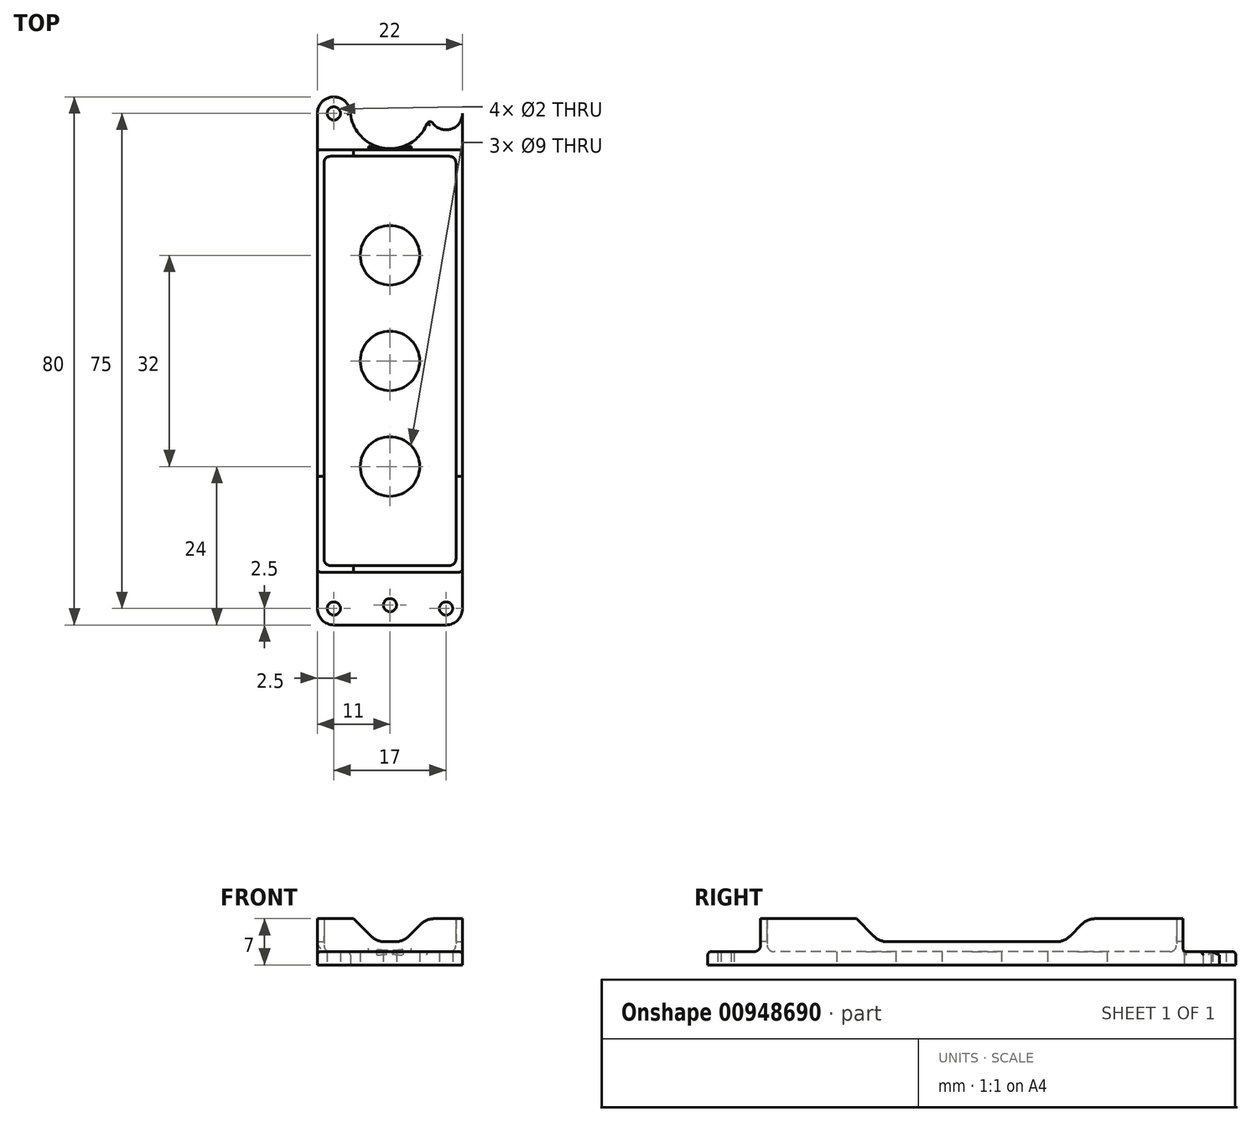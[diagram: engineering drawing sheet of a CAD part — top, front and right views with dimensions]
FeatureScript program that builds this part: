
annotation { "Feature Type Name" : "Feature", "Feature Type Description" : "" }
export const myFeature = defineFeature(function(context is Context, id is Id, definition is map)
    precondition{}
    {
        {
            var Q0;
            Q0=qCreatedBy(makeId("Top.planeOp"),FACE);
            var sketch = newSketch(context, id + "F0", { "sketchPlane" : qUnion([Q0])});
            skPoint(sketch, "E0.middle", {"position": v(0, 0) * mm});
            skPoint(sketch, "E1", {"position": v(-8, 8) * mm});
            skPoint(sketch, "E2", {"position": v(8, 8) * mm});
            skPoint(sketch, "E3", {"position": v(8, -8) * mm});
            skPoint(sketch, "E4", {"position": v(-8, -8) * mm});
            skLineSegment(sketch, "E5", {"start": v(0, -40) * mm, "end": v(8.5, -40) * mm});
            skLineSegment(sketch, "E6", {"start": v(11, -37.5) * mm, "end": v(11, -25.31) * mm});
            skLineSegment(sketch, "E7", {"start": v(-11, 37.5) * mm, "end": v(-11, 25.31) * mm});
            skLineSegment(sketch, "E8", {"start": v(-8.5, -40) * mm, "end": v(0, -40) * mm});
            skLineSegment(sketch, "E9.trimOffspring", {"start": v(11, 25.31) * mm, "end": v(11, 37.5) * mm});
            skLineSegment(sketch, "E10.trimOffspring", {"start": v(-11, -25.31) * mm, "end": v(-11, -37.5) * mm});
            skArc(sketch, "E11.filletArc", {"start": v(-8.5, 40) * mm, "mid": v(-10.27, 39.27) * mm, "end": v(-11, 37.5) * mm});
            skPoint(sketch, "E12.visualSharp", {"position": v(11, 40) * mm});
            skArc(sketch, "E12.filletArc", {"start": v(11, 37.5) * mm, "mid": v(10.27, 39.27) * mm, "end": v(8.5, 40) * mm});
            skArc(sketch, "E13.filletArc", {"start": v(-11, -37.5) * mm, "mid": v(-10.27, -39.27) * mm, "end": v(-8.5, -40) * mm});
            skPoint(sketch, "E14.visualSharp", {"position": v(11, -40) * mm});
            skArc(sketch, "E14.filletArc", {"start": v(8.5, -40) * mm, "mid": v(10.27, -39.27) * mm, "end": v(11, -37.5) * mm});
            skCircle(sketch, "E15", {"center": v(-8.5, 37.5) * mm, "radius": 2.5 * mm});
            skCircle(sketch, "E16", {"center": v(8.5, 37.5) * mm, "radius": 2.5 * mm});
            skCircle(sketch, "E17", {"center": v(-8.5, -37.5) * mm, "radius": 2.5 * mm});
            skCircle(sketch, "E18", {"center": v(8.5, -37.5) * mm, "radius": 2.5 * mm});
            skPoint(sketch, "E19", {"position": v(0, 30) * mm});
            skPoint(sketch, "E20", {"position": v(0, 16) * mm});
            skPoint(sketch, "E21.MirrorP", {"position": v(0, -16) * mm});
            skPoint(sketch, "E22.MirrorP", {"position": v(0, -30) * mm});
            skLineSegment(sketch, "E23", {"start": v(-11, 25.31) * mm, "end": v(-11, -25.31) * mm});
            skLineSegment(sketch, "E24", {"start": v(11, 25.31) * mm, "end": v(11, -25.31) * mm});
            skArc(sketch, "E25", {"start": v(-6, 37.43) * mm, "mid": v(0, 32.15) * mm, "end": v(6, 37.43) * mm});
            skPoint(sketch, "E25.centerSnap0", {"position": v(0, 40) * mm});
            skLineSegment(sketch, "E26", {"start": v(0, -32) * mm, "end": v(11, -32) * mm});
            skLineSegment(sketch, "E27", {"start": v(0, -32) * mm, "end": v(-11, -32) * mm});
            skLineSegment(sketch, "E28", {"start": v(0, 32) * mm, "end": v(11, 32) * mm});
            skLineSegment(sketch, "E29", {"start": v(0, 32) * mm, "end": v(-11, 32) * mm});
            skLineSegment(sketch, "E30", {"start": v(0, -31) * mm, "end": v(10, -31) * mm});
            skLineSegment(sketch, "E31", {"start": v(10, -31) * mm, "end": v(10, 31) * mm});
            skLineSegment(sketch, "E32", {"start": v(10, 31) * mm, "end": v(-10, 31) * mm});
            skLineSegment(sketch, "E33", {"start": v(-10, 31) * mm, "end": v(-10, -31) * mm});
            skLineSegment(sketch, "E34", {"start": v(-10, -31) * mm, "end": v(0, -31) * mm});
            skPoint(sketch, "E35", {"position": v(0, -37) * mm});
            skSolve(sketch);
        }
        {
            var Q0;
            {var subQ0=sQuery(id+"F0.wireOp",EDGE,"E15");var subQ1=makeQuery(id+"F0.imprint","INTERSECT",VERTEX,{"derivedFrom":[sQuery(id+"F0.wireOp",EDGE,"E7"),subQ0]});Q0=makeQuery(id+"F0.imprint","IMPRINT",FACE,{"disambiguationData":[TD([[makeQuery(id+"F0.imprint","IMPRINT",EDGE,{"disambiguationData":[TD([[subQ1,-1.0]])],"derivedFrom":subQ0}),1.0]])]});}
            var Q1;
            {var subQ3=sQuery(id+"F0.wireOp",EDGE,"E25");Q1=makeQuery(id+"F0.imprint","IMPRINT",FACE,{"disambiguationData":[TD([[makeQuery(id+"F0.imprint","IMPRINT",EDGE,{"derivedFrom":subQ3}),-1.0]])]});}
            var Q2;
            {var subQ0=sQuery(id+"F0.wireOp",EDGE,"E16");var subQ1=makeQuery(id+"F0.imprint","INTERSECT",VERTEX,{"derivedFrom":[sQuery(id+"F0.wireOp",EDGE,"E9.trimOffspring"),subQ0]});Q2=makeQuery(id+"F0.imprint","IMPRINT",FACE,{"disambiguationData":[TD([[makeQuery(id+"F0.imprint","IMPRINT",EDGE,{"disambiguationData":[TD([[subQ1,-1.0]])],"derivedFrom":subQ0}),1.0]])]});}
            var Q3;
            {var subQ3=sQuery(id+"F0.wireOp",EDGE,"E23");Q3=makeQuery(id+"F0.imprint","IMPRINT",FACE,{"disambiguationData":[TD([[makeQuery(id+"F0.imprint","IMPRINT",EDGE,{"derivedFrom":subQ3}),1.0]])]});}
            var Q4;
            Q4=makeQuery(id+"F0.imprint","IMPRINT",FACE,{"disambiguationData":[TD([[makeQuery(id+"F0.imprint","IMPRINT",EDGE,{"derivedFrom":sQuery(id+"F0.wireOp",EDGE,"E30")}),1.0]])]});
            var Q5;
            {var subQ9=sQuery(id+"F0.wireOp",EDGE,"E5");Q5=makeQuery(id+"F0.imprint","IMPRINT",FACE,{"disambiguationData":[TD([[makeQuery(id+"F0.imprint","IMPRINT",EDGE,{"derivedFrom":subQ9}),1.0]])]});}
            var Q6;
            {var subQ0=sQuery(id+"F0.wireOp",EDGE,"E17");var subQ1=makeQuery(id+"F0.imprint","INTERSECT",VERTEX,{"derivedFrom":[sQuery(id+"F0.wireOp",EDGE,"E8"),subQ0]});Q6=makeQuery(id+"F0.imprint","IMPRINT",FACE,{"disambiguationData":[TD([[makeQuery(id+"F0.imprint","IMPRINT",EDGE,{"disambiguationData":[TD([[subQ1,1.0]])],"derivedFrom":subQ0}),1.0]])]});}
            var Q7;
            {var subQ0=sQuery(id+"F0.wireOp",EDGE,"E18");var subQ1=makeQuery(id+"F0.imprint","INTERSECT",VERTEX,{"derivedFrom":[sQuery(id+"F0.wireOp",EDGE,"E5"),subQ0]});Q7=makeQuery(id+"F0.imprint","IMPRINT",FACE,{"disambiguationData":[TD([[makeQuery(id+"F0.imprint","IMPRINT",EDGE,{"disambiguationData":[TD([[subQ1,1.0]])],"derivedFrom":subQ0}),1.0]])]});}
            extrude(context, id + "F1", {"entities" : qUnion([Q0, Q1, Q2, Q3, Q4, Q5, Q6, Q7]), "depth" : 2 * mm, "offsetDistance" : 25 * mm});
        }
        {
            var Q0;
            {var subQ3=sQuery(id+"F0.wireOp",EDGE,"E23");Q0=makeQuery(id+"F0.imprint","IMPRINT",FACE,{"disambiguationData":[TD([[makeQuery(id+"F0.imprint","IMPRINT",EDGE,{"derivedFrom":subQ3}),1.0]])]});}
            extrude(context, id + "F2", {"entities" : qUnion([Q0]), "operationType" : NewBodyOperationType.ADD, "depth" : 7 * mm, "offsetDistance" : 25 * mm});
        }
        {
            var Q0;
            Q0=makeQuery(id+"F1.opExtrude","CAP_EDGE",EDGE,{"disambiguationData":[OSD([sQuery(id+"F0.wireOp",EDGE,"E25")])],"isStart":false});
            fillet(context, id + "F3", {"entities" : qUnion([Q0]), "radius" : 0.5 * mm, "tangentPropagation" : true, "allowEdgeOverflow" : false});
        }
        {
            var Q0;
            Q0=makeQuery(id+"F2.boolean.opBoolean","INTERSECT",EDGE,{"derivedFrom":[makeQuery(id+"F1.opExtrude","CAP_FACE",FACE,{"disambiguationData":[OSD([sQuery(id+"F0.wireOp",EDGE,"E5"),sQuery(id+"F0.wireOp",EDGE,"E6"),sQuery(id+"F0.wireOp",EDGE,"E7"),sQuery(id+"F0.wireOp",EDGE,"E8"),sQuery(id+"F0.wireOp",EDGE,"E9.trimOffspring"),sQuery(id+"F0.wireOp",EDGE,"E10.trimOffspring"),sQuery(id+"F0.wireOp",EDGE,"E15"),sQuery(id+"F0.wireOp",EDGE,"E16"),sQuery(id+"F0.wireOp",EDGE,"E17"),sQuery(id+"F0.wireOp",EDGE,"E18"),sQuery(id+"F0.wireOp",EDGE,"E23"),sQuery(id+"F0.wireOp",EDGE,"E24"),sQuery(id+"F0.wireOp",EDGE,"E25")])],"isStart":false}),makeQuery(id+"F2.opExtrude","SWEPT_FACE",FACE,{"disambiguationData":[OSD([sQuery(id+"F0.wireOp",EDGE,"E26"),sQuery(id+"F0.wireOp",EDGE,"E27")])]})]});
            var Q1;
            Q1=makeQuery(id+"F2.opExtrude","SWEPT_EDGE",EDGE,{"disambiguationData":[OSD([sQuery(id+"F0.wireOp",EDGE,"E33"),sQuery(id+"F0.wireOp",EDGE,"E34")])]});
            var Q2;
            Q2=makeQuery(id+"F2.opExtrude","SWEPT_EDGE",EDGE,{"disambiguationData":[OSD([sQuery(id+"F0.wireOp",EDGE,"E30"),sQuery(id+"F0.wireOp",EDGE,"E31")])]});
            var Q3;
            Q3=makeQuery(id+"F2.boolean.opBoolean","INTERSECT",EDGE,{"derivedFrom":[makeQuery(id+"F1.opExtrude","CAP_FACE",FACE,{"disambiguationData":[OSD([sQuery(id+"F0.wireOp",EDGE,"E5"),sQuery(id+"F0.wireOp",EDGE,"E6"),sQuery(id+"F0.wireOp",EDGE,"E7"),sQuery(id+"F0.wireOp",EDGE,"E8"),sQuery(id+"F0.wireOp",EDGE,"E9.trimOffspring"),sQuery(id+"F0.wireOp",EDGE,"E10.trimOffspring"),sQuery(id+"F0.wireOp",EDGE,"E15"),sQuery(id+"F0.wireOp",EDGE,"E16"),sQuery(id+"F0.wireOp",EDGE,"E17"),sQuery(id+"F0.wireOp",EDGE,"E18"),sQuery(id+"F0.wireOp",EDGE,"E23"),sQuery(id+"F0.wireOp",EDGE,"E24"),sQuery(id+"F0.wireOp",EDGE,"E25")])],"isStart":false}),makeQuery(id+"F2.opExtrude","SWEPT_FACE",FACE,{"disambiguationData":[OSD([sQuery(id+"F0.wireOp",EDGE,"E30"),sQuery(id+"F0.wireOp",EDGE,"E34")])]})]});
            var Q4;
            Q4=makeQuery(id+"F2.boolean.opBoolean","INTERSECT",EDGE,{"derivedFrom":[makeQuery(id+"F1.opExtrude","CAP_FACE",FACE,{"disambiguationData":[OSD([sQuery(id+"F0.wireOp",EDGE,"E5"),sQuery(id+"F0.wireOp",EDGE,"E6"),sQuery(id+"F0.wireOp",EDGE,"E7"),sQuery(id+"F0.wireOp",EDGE,"E8"),sQuery(id+"F0.wireOp",EDGE,"E9.trimOffspring"),sQuery(id+"F0.wireOp",EDGE,"E10.trimOffspring"),sQuery(id+"F0.wireOp",EDGE,"E15"),sQuery(id+"F0.wireOp",EDGE,"E16"),sQuery(id+"F0.wireOp",EDGE,"E17"),sQuery(id+"F0.wireOp",EDGE,"E18"),sQuery(id+"F0.wireOp",EDGE,"E23"),sQuery(id+"F0.wireOp",EDGE,"E24"),sQuery(id+"F0.wireOp",EDGE,"E25")])],"isStart":false}),makeQuery(id+"F2.opExtrude","SWEPT_FACE",FACE,{"disambiguationData":[OSD([sQuery(id+"F0.wireOp",EDGE,"E33")])]})]});
            var Q5;
            Q5=makeQuery(id+"F2.boolean.opBoolean","INTERSECT",EDGE,{"derivedFrom":[makeQuery(id+"F1.opExtrude","CAP_FACE",FACE,{"disambiguationData":[OSD([sQuery(id+"F0.wireOp",EDGE,"E5"),sQuery(id+"F0.wireOp",EDGE,"E6"),sQuery(id+"F0.wireOp",EDGE,"E7"),sQuery(id+"F0.wireOp",EDGE,"E8"),sQuery(id+"F0.wireOp",EDGE,"E9.trimOffspring"),sQuery(id+"F0.wireOp",EDGE,"E10.trimOffspring"),sQuery(id+"F0.wireOp",EDGE,"E15"),sQuery(id+"F0.wireOp",EDGE,"E16"),sQuery(id+"F0.wireOp",EDGE,"E17"),sQuery(id+"F0.wireOp",EDGE,"E18"),sQuery(id+"F0.wireOp",EDGE,"E23"),sQuery(id+"F0.wireOp",EDGE,"E24"),sQuery(id+"F0.wireOp",EDGE,"E25")])],"isStart":false}),makeQuery(id+"F2.opExtrude","SWEPT_FACE",FACE,{"disambiguationData":[OSD([sQuery(id+"F0.wireOp",EDGE,"E31")])]})]});
            var Q6;
            Q6=makeQuery(id+"F2.opExtrude","SWEPT_EDGE",EDGE,{"disambiguationData":[OSD([sQuery(id+"F0.wireOp",EDGE,"E31"),sQuery(id+"F0.wireOp",EDGE,"E32")])]});
            var Q7;
            Q7=makeQuery(id+"F2.boolean.opBoolean","INTERSECT",EDGE,{"derivedFrom":[makeQuery(id+"F1.opExtrude","CAP_FACE",FACE,{"disambiguationData":[OSD([sQuery(id+"F0.wireOp",EDGE,"E5"),sQuery(id+"F0.wireOp",EDGE,"E6"),sQuery(id+"F0.wireOp",EDGE,"E7"),sQuery(id+"F0.wireOp",EDGE,"E8"),sQuery(id+"F0.wireOp",EDGE,"E9.trimOffspring"),sQuery(id+"F0.wireOp",EDGE,"E10.trimOffspring"),sQuery(id+"F0.wireOp",EDGE,"E15"),sQuery(id+"F0.wireOp",EDGE,"E16"),sQuery(id+"F0.wireOp",EDGE,"E17"),sQuery(id+"F0.wireOp",EDGE,"E18"),sQuery(id+"F0.wireOp",EDGE,"E23"),sQuery(id+"F0.wireOp",EDGE,"E24"),sQuery(id+"F0.wireOp",EDGE,"E25")])],"isStart":false}),makeQuery(id+"F2.opExtrude","SWEPT_FACE",FACE,{"disambiguationData":[OSD([sQuery(id+"F0.wireOp",EDGE,"E32")])]})]});
            var Q8;
            Q8=makeQuery(id+"F2.opExtrude","SWEPT_EDGE",EDGE,{"disambiguationData":[OSD([sQuery(id+"F0.wireOp",EDGE,"E32"),sQuery(id+"F0.wireOp",EDGE,"E33")])]});
            fillet(context, id + "F4", {"entities" : qUnion([Q0, Q1, Q2, Q3, Q4, Q5, Q6, Q7, Q8]), "radius" : 1 * mm, "tangentPropagation" : true, "allowEdgeOverflow" : false});
        }
        {
            var Q0;
            Q0=makeQuery(id+"F1.opExtrude","CAP_EDGE",EDGE,{"disambiguationData":[OSD([sQuery(id+"F0.wireOp",EDGE,"E15")])],"isStart":false});
            var Q1;
            Q1=makeQuery(id+"F1.opExtrude","CAP_EDGE",EDGE,{"disambiguationData":[OSD([sQuery(id+"F0.wireOp",EDGE,"E16")])],"isStart":false});
            var Q2;
            Q2=makeQuery(id+"F1.opExtrude","CAP_EDGE",EDGE,{"disambiguationData":[OSD([sQuery(id+"F0.wireOp",EDGE,"E5"),sQuery(id+"F0.wireOp",EDGE,"E8")])],"isStart":false});
            var Q3;
            Q3=makeQuery(id+"F2.boolean.opBoolean","INTERSECT",EDGE,{"derivedFrom":[makeQuery(id+"F1.opExtrude","CAP_FACE",FACE,{"disambiguationData":[OSD([sQuery(id+"F0.wireOp",EDGE,"E5"),sQuery(id+"F0.wireOp",EDGE,"E6"),sQuery(id+"F0.wireOp",EDGE,"E7"),sQuery(id+"F0.wireOp",EDGE,"E8"),sQuery(id+"F0.wireOp",EDGE,"E9.trimOffspring"),sQuery(id+"F0.wireOp",EDGE,"E10.trimOffspring"),sQuery(id+"F0.wireOp",EDGE,"E15"),sQuery(id+"F0.wireOp",EDGE,"E16"),sQuery(id+"F0.wireOp",EDGE,"E17"),sQuery(id+"F0.wireOp",EDGE,"E18"),sQuery(id+"F0.wireOp",EDGE,"E23"),sQuery(id+"F0.wireOp",EDGE,"E24"),sQuery(id+"F0.wireOp",EDGE,"E25")])],"isStart":false}),makeQuery(id+"F2.opExtrude","SWEPT_FACE",FACE,{"disambiguationData":[OSD([sQuery(id+"F0.wireOp",EDGE,"E28"),sQuery(id+"F0.wireOp",EDGE,"E29")])]})]});
            fillet(context, id + "F5", {"entities" : qUnion([Q0, Q1, Q2, Q3]), "radius" : 0.5 * mm, "tangentPropagation" : true, "allowEdgeOverflow" : false});
        }
        {
            var Q0;
            {var subQ0=sQuery(id+"F0.wireOp",EDGE,"E23");var subQ1=sQuery(id+"F0.wireOp",EDGE,"E10.trimOffspring");var subQ2=sQuery(id+"F0.wireOp",EDGE,"E7");Q0=makeQuery(id+"F2.boolean.opBoolean","MERGE",FACE,{"derivedFrom":[makeQuery(id+"F1.opExtrude","SWEPT_FACE",FACE,{"disambiguationData":[OSD([subQ2,subQ1,subQ0])]}),makeQuery(id+"F2.opExtrude","SWEPT_FACE",FACE,{"disambiguationData":[OSD([subQ2,subQ1,subQ0])]})]});}
            var sketch = newSketch(context, id + "F6", { "sketchPlane" : qUnion([Q0])});
            skLineSegment(sketch, "E36", {"start": v(0, 0) * mm, "end": v(0, 3.5) * mm});
            skLineSegment(sketch, "E37", {"start": v(0, 3.5) * mm, "end": v(14, 3.5) * mm});
            skLineSegment(sketch, "E38", {"start": v(17.5, 7) * mm, "end": v(14, 3.5) * mm});
            skLineSegment(sketch, "E39.MirrorCS", {"start": v(0, 3.5) * mm, "end": v(-14, 3.5) * mm});
            skLineSegment(sketch, "E40.MirrorCS", {"start": v(-17.5, 7) * mm, "end": v(-14, 3.5) * mm});
            skSolve(sketch);
        }
        {
            var Q0;
            Q0=makeQuery(id+"F6.imprint","IMPRINT",FACE,{"disambiguationData":[TD([[makeQuery(id+"F6.imprint","IMPRINT",EDGE,{"derivedFrom":sQuery(id+"F6.wireOp",EDGE,"E37")}),1.0]])]});
            extrude(context, id + "F7", {"entities" : qUnion([Q0]), "operationType" : NewBodyOperationType.REMOVE, "depth" : 25 * mm, "offsetDistance" : 25 * mm, "hasSecondDirection" : true, "secondDirectionOppositeDirection" : true, "secondDirectionDepth" : 25 * mm});
        }
        {
            var Q0;
            Q0=makeQuery(id+"F2.opExtrude","SWEPT_FACE",FACE,{"disambiguationData":[OSD([sQuery(id+"F0.wireOp",EDGE,"E26"),sQuery(id+"F0.wireOp",EDGE,"E27")])]});
            var sketch = newSketch(context, id + "F8", { "sketchPlane" : qUnion([Q0])});
            skLineSegment(sketch, "E41", {"start": v(0, 0) * mm, "end": v(0, 3.5) * mm});
            skLineSegment(sketch, "E42", {"start": v(0, 3.5) * mm, "end": v(2, 3.5) * mm});
            skLineSegment(sketch, "E43", {"start": v(5.5, 7) * mm, "end": v(2, 3.5) * mm});
            skLineSegment(sketch, "E44.MirrorCS", {"start": v(-5.5, 7) * mm, "end": v(-2, 3.5) * mm});
            skLineSegment(sketch, "E45.MirrorCS", {"start": v(0, 3.5) * mm, "end": v(-2, 3.5) * mm});
            skSolve(sketch);
        }
        {
            var Q0;
            Q0=makeQuery(id+"F8.imprint","IMPRINT",FACE,{"disambiguationData":[TD([[makeQuery(id+"F8.imprint","IMPRINT",EDGE,{"derivedFrom":sQuery(id+"F8.wireOp",EDGE,"E42")}),1.0]])]});
            extrude(context, id + "F9", {"entities" : qUnion([Q0]), "operationType" : NewBodyOperationType.REMOVE, "oppositeDirection" : true, "depth" : 80 * mm, "offsetDistance" : 25 * mm, "hasSecondDirection" : true, "secondDirectionOppositeDirection" : false, "secondDirectionDepth" : 25 * mm});
        }
        {
            var Q0;
            {var subQ0=sQuery(id+"F8.wireOp",EDGE,"E45.MirrorCS");var subQ1=sQuery(id+"F8.wireOp",EDGE,"E44.MirrorCS");Q0=makeQuery(id+"F9.boolean.opBoolean","COPY",EDGE,{"disambiguationData":[TD([makeQuery(id+"F2.opExtrude","SWEPT_FACE",FACE,{"disambiguationData":[OSD([sQuery(id+"F0.wireOp",EDGE,"E26"),sQuery(id+"F0.wireOp",EDGE,"E27")])]})])],"derivedFrom":makeQuery(id+"F9.opExtrude","SWEPT_EDGE",EDGE,{"disambiguationData":[OSD([subQ1,subQ0])]})});}
            var Q1;
            {var subQ0=sQuery(id+"F8.wireOp",EDGE,"E43");var subQ1=sQuery(id+"F8.wireOp",EDGE,"E42");Q1=makeQuery(id+"F9.boolean.opBoolean","COPY",EDGE,{"disambiguationData":[TD([makeQuery(id+"F2.opExtrude","SWEPT_FACE",FACE,{"disambiguationData":[OSD([sQuery(id+"F0.wireOp",EDGE,"E26"),sQuery(id+"F0.wireOp",EDGE,"E27")])]})])],"derivedFrom":makeQuery(id+"F9.opExtrude","SWEPT_EDGE",EDGE,{"disambiguationData":[OSD([subQ1,subQ0])]})});}
            var Q2;
            {var subQ2=sQuery(id+"F0.wireOp",EDGE,"E27");var subQ3=sQuery(id+"F0.wireOp",EDGE,"E26");var subQ4=sQuery(id+"F8.wireOp",EDGE,"E43");Q2=makeQuery(id+"F9.boolean.opBoolean","COPY",EDGE,{"disambiguationData":[TD([makeQuery(id+"F2.opExtrude","SWEPT_FACE",FACE,{"disambiguationData":[OSD([subQ3,subQ2])]})])],"derivedFrom":makeQuery(id+"F9.opExtrude","SWEPT_EDGE",EDGE,{"disambiguationData":[OSD([subQ3,subQ2,subQ4])]})});}
            var Q3;
            {var subQ2=sQuery(id+"F0.wireOp",EDGE,"E27");var subQ3=sQuery(id+"F0.wireOp",EDGE,"E26");var subQ4=sQuery(id+"F8.wireOp",EDGE,"E44.MirrorCS");Q3=makeQuery(id+"F9.boolean.opBoolean","COPY",EDGE,{"disambiguationData":[TD([makeQuery(id+"F2.opExtrude","SWEPT_FACE",FACE,{"disambiguationData":[OSD([subQ3,subQ2])]})])],"derivedFrom":makeQuery(id+"F9.opExtrude","SWEPT_EDGE",EDGE,{"disambiguationData":[OSD([subQ3,subQ2,subQ4])]})});}
            var Q4;
            {var subQ0=sQuery(id+"F0.wireOp",EDGE,"E31");var subQ2=sQuery(id+"F0.wireOp",EDGE,"E23");var subQ3=sQuery(id+"F0.wireOp",EDGE,"E10.trimOffspring");var subQ5=sQuery(id+"F0.wireOp",EDGE,"E7");var subQ7=sQuery(id+"F6.wireOp",EDGE,"E38");Q4=makeQuery(id+"F7.boolean.opBoolean","COPY",EDGE,{"disambiguationData":[TD([makeQuery(id+"F2.opExtrude","SWEPT_FACE",FACE,{"disambiguationData":[OSD([subQ0])]})])],"derivedFrom":makeQuery(id+"F7.opExtrude","SWEPT_EDGE",EDGE,{"disambiguationData":[OSD([subQ5,subQ3,subQ2,subQ7])]})});}
            var Q5;
            {var subQ0=sQuery(id+"F6.wireOp",EDGE,"E37");var subQ4=sQuery(id+"F6.wireOp",EDGE,"E38");Q5=makeQuery(id+"F7.boolean.opBoolean","COPY",EDGE,{"disambiguationData":[TD([makeQuery(id+"F2.opExtrude","SWEPT_FACE",FACE,{"disambiguationData":[OSD([sQuery(id+"F0.wireOp",EDGE,"E31")])]})])],"derivedFrom":makeQuery(id+"F7.opExtrude","SWEPT_EDGE",EDGE,{"disambiguationData":[OSD([subQ0,subQ4])]})});}
            var Q6;
            {var subQ0=sQuery(id+"F6.wireOp",EDGE,"E39.MirrorCS");var subQ4=sQuery(id+"F6.wireOp",EDGE,"E40.MirrorCS");Q6=makeQuery(id+"F7.boolean.opBoolean","COPY",EDGE,{"disambiguationData":[TD([makeQuery(id+"F2.opExtrude","SWEPT_FACE",FACE,{"disambiguationData":[OSD([sQuery(id+"F0.wireOp",EDGE,"E31")])]})])],"derivedFrom":makeQuery(id+"F7.opExtrude","SWEPT_EDGE",EDGE,{"disambiguationData":[OSD([subQ0,subQ4])]})});}
            var Q7;
            {var subQ0=sQuery(id+"F0.wireOp",EDGE,"E31");var subQ2=sQuery(id+"F0.wireOp",EDGE,"E23");var subQ3=sQuery(id+"F0.wireOp",EDGE,"E10.trimOffspring");var subQ5=sQuery(id+"F0.wireOp",EDGE,"E7");var subQ7=sQuery(id+"F6.wireOp",EDGE,"E40.MirrorCS");Q7=makeQuery(id+"F7.boolean.opBoolean","COPY",EDGE,{"disambiguationData":[TD([makeQuery(id+"F2.opExtrude","SWEPT_FACE",FACE,{"disambiguationData":[OSD([subQ0])]})])],"derivedFrom":makeQuery(id+"F7.opExtrude","SWEPT_EDGE",EDGE,{"disambiguationData":[OSD([subQ5,subQ3,subQ2,subQ7])]})});}
            var Q8;
            {var subQ0=sQuery(id+"F0.wireOp",EDGE,"E32");var subQ3=sQuery(id+"F0.wireOp",EDGE,"E27");var subQ4=sQuery(id+"F0.wireOp",EDGE,"E26");var subQ5=sQuery(id+"F8.wireOp",EDGE,"E44.MirrorCS");Q8=makeQuery(id+"F9.boolean.opBoolean","COPY",EDGE,{"disambiguationData":[TD([makeQuery(id+"F2.opExtrude","SWEPT_FACE",FACE,{"disambiguationData":[OSD([subQ0])]})])],"derivedFrom":makeQuery(id+"F9.opExtrude","SWEPT_EDGE",EDGE,{"disambiguationData":[OSD([subQ4,subQ3,subQ5])]})});}
            var Q9;
            {var subQ0=sQuery(id+"F8.wireOp",EDGE,"E44.MirrorCS");var subQ1=sQuery(id+"F8.wireOp",EDGE,"E45.MirrorCS");Q9=makeQuery(id+"F9.boolean.opBoolean","COPY",EDGE,{"disambiguationData":[TD([makeQuery(id+"F2.opExtrude","SWEPT_FACE",FACE,{"disambiguationData":[OSD([sQuery(id+"F0.wireOp",EDGE,"E32")])]})])],"derivedFrom":makeQuery(id+"F9.opExtrude","SWEPT_EDGE",EDGE,{"disambiguationData":[OSD([subQ0,subQ1])]})});}
            var Q10;
            {var subQ0=sQuery(id+"F8.wireOp",EDGE,"E42");var subQ1=sQuery(id+"F8.wireOp",EDGE,"E43");Q10=makeQuery(id+"F9.boolean.opBoolean","COPY",EDGE,{"disambiguationData":[TD([makeQuery(id+"F2.opExtrude","SWEPT_FACE",FACE,{"disambiguationData":[OSD([sQuery(id+"F0.wireOp",EDGE,"E32")])]})])],"derivedFrom":makeQuery(id+"F9.opExtrude","SWEPT_EDGE",EDGE,{"disambiguationData":[OSD([subQ0,subQ1])]})});}
            var Q11;
            {var subQ0=sQuery(id+"F0.wireOp",EDGE,"E32");var subQ3=sQuery(id+"F0.wireOp",EDGE,"E27");var subQ4=sQuery(id+"F0.wireOp",EDGE,"E26");var subQ5=sQuery(id+"F8.wireOp",EDGE,"E43");Q11=makeQuery(id+"F9.boolean.opBoolean","COPY",EDGE,{"disambiguationData":[TD([makeQuery(id+"F2.opExtrude","SWEPT_FACE",FACE,{"disambiguationData":[OSD([subQ0])]})])],"derivedFrom":makeQuery(id+"F9.opExtrude","SWEPT_EDGE",EDGE,{"disambiguationData":[OSD([subQ4,subQ3,subQ5])]})});}
            var Q12;
            {var subQ0=sQuery(id+"F0.wireOp",EDGE,"E33");var subQ1=sQuery(id+"F0.wireOp",EDGE,"E23");var subQ2=sQuery(id+"F0.wireOp",EDGE,"E10.trimOffspring");var subQ3=sQuery(id+"F0.wireOp",EDGE,"E7");var subQ4=sQuery(id+"F6.wireOp",EDGE,"E40.MirrorCS");Q12=makeQuery(id+"F7.boolean.opBoolean","COPY",EDGE,{"disambiguationData":[TD([makeQuery(id+"F2.opExtrude","SWEPT_FACE",FACE,{"disambiguationData":[OSD([subQ0])]})])],"derivedFrom":makeQuery(id+"F7.opExtrude","SWEPT_EDGE",EDGE,{"disambiguationData":[OSD([subQ3,subQ2,subQ1,subQ4])]})});}
            var Q13;
            {var subQ0=sQuery(id+"F6.wireOp",EDGE,"E39.MirrorCS");var subQ4=sQuery(id+"F6.wireOp",EDGE,"E40.MirrorCS");Q13=makeQuery(id+"F7.boolean.opBoolean","COPY",EDGE,{"disambiguationData":[TD([makeQuery(id+"F2.opExtrude","SWEPT_FACE",FACE,{"disambiguationData":[OSD([sQuery(id+"F0.wireOp",EDGE,"E33")])]})])],"derivedFrom":makeQuery(id+"F7.opExtrude","SWEPT_EDGE",EDGE,{"disambiguationData":[OSD([subQ0,subQ4])]})});}
            var Q14;
            {var subQ0=sQuery(id+"F6.wireOp",EDGE,"E37");var subQ1=sQuery(id+"F6.wireOp",EDGE,"E38");Q14=makeQuery(id+"F7.boolean.opBoolean","COPY",EDGE,{"disambiguationData":[TD([makeQuery(id+"F2.opExtrude","SWEPT_FACE",FACE,{"disambiguationData":[OSD([sQuery(id+"F0.wireOp",EDGE,"E33")])]})])],"derivedFrom":makeQuery(id+"F7.opExtrude","SWEPT_EDGE",EDGE,{"disambiguationData":[OSD([subQ0,subQ1])]})});}
            var Q15;
            {var subQ0=sQuery(id+"F0.wireOp",EDGE,"E33");var subQ1=sQuery(id+"F6.wireOp",EDGE,"E38");var subQ2=sQuery(id+"F0.wireOp",EDGE,"E23");var subQ3=sQuery(id+"F0.wireOp",EDGE,"E10.trimOffspring");var subQ4=sQuery(id+"F0.wireOp",EDGE,"E7");Q15=makeQuery(id+"F7.boolean.opBoolean","COPY",EDGE,{"disambiguationData":[TD([makeQuery(id+"F2.opExtrude","SWEPT_FACE",FACE,{"disambiguationData":[OSD([subQ0])]})])],"derivedFrom":makeQuery(id+"F7.opExtrude","SWEPT_EDGE",EDGE,{"disambiguationData":[OSD([subQ4,subQ3,subQ2,subQ1])]})});}
            fillet(context, id + "F10", {"entities" : qUnion([Q0, Q1, Q2, Q3, Q4, Q5, Q6, Q7, Q8, Q9, Q10, Q11, Q12, Q13, Q14, Q15]), "radius" : 3 * mm, "tangentPropagation" : true, "allowEdgeOverflow" : false});
        }
        {
            var Q0;
            Q0=sQuery(id+"F0.wireOp",VERTEX,"E12.filletArc.center");
            var Q1;
            Q1=sQuery(id+"F0.wireOp",VERTEX,"E11.filletArc.center");
            var Q2;
            Q2=sQuery(id+"F0.wireOp",VERTEX,"E14.filletArc.center");
            var Q3;
            Q3=sQuery(id+"F0.wireOp",VERTEX,"E13.filletArc.center");
            var Q4;
            Q4=sQuery(id+"F0.wireOp",VERTEX,"E35");
            var Q5;
            Q5=makeQuery(id+"F1.opExtrude","SWEPT_BODY",BODY,{"disambiguationData":[OSD([sQuery(id+"F0.wireOp",EDGE,"E5"),sQuery(id+"F0.wireOp",EDGE,"E6"),sQuery(id+"F0.wireOp",EDGE,"E7"),sQuery(id+"F0.wireOp",EDGE,"E8"),sQuery(id+"F0.wireOp",EDGE,"E9.trimOffspring"),sQuery(id+"F0.wireOp",EDGE,"E10.trimOffspring"),sQuery(id+"F0.wireOp",EDGE,"E15"),sQuery(id+"F0.wireOp",EDGE,"E16"),sQuery(id+"F0.wireOp",EDGE,"E17"),sQuery(id+"F0.wireOp",EDGE,"E18"),sQuery(id+"F0.wireOp",EDGE,"E23"),sQuery(id+"F0.wireOp",EDGE,"E24"),sQuery(id+"F0.wireOp",EDGE,"E25")])]});
            hole(context, id + "F11", {"style" : HoleStyle.SIMPLE, "endStyle" : HoleEndStyle.BLIND, "oppositeDirection" : true, "holeDiameter" : 2 * mm, "majorDiameter" : 5 * mm, "holeDepth" : 7 * mm, "isTappedThrough" : true, "tappedDepth" : 12 * mm, "tapClearance" : 3, "startFromSketch" : true, "locations" : qUnion([Q0, Q1, Q2, Q3, Q4]), "scope" : qUnion([Q5])});
        }
        {
            var Q0;
            Q0=sQuery(id+"F0.wireOp",VERTEX,"E20");
            var Q1;
            Q1=sQuery(id+"F0.wireOp",VERTEX,"E21.MirrorP");
            var Q2;
            Q2=sQuery(id+"F0.wireOp",VERTEX,"E0.middle");
            var Q3;
            Q3=makeQuery(id+"F1.opExtrude","SWEPT_BODY",BODY,{"disambiguationData":[OSD([sQuery(id+"F0.wireOp",EDGE,"E5"),sQuery(id+"F0.wireOp",EDGE,"E6"),sQuery(id+"F0.wireOp",EDGE,"E7"),sQuery(id+"F0.wireOp",EDGE,"E8"),sQuery(id+"F0.wireOp",EDGE,"E9.trimOffspring"),sQuery(id+"F0.wireOp",EDGE,"E10.trimOffspring"),sQuery(id+"F0.wireOp",EDGE,"E15"),sQuery(id+"F0.wireOp",EDGE,"E16"),sQuery(id+"F0.wireOp",EDGE,"E17"),sQuery(id+"F0.wireOp",EDGE,"E18"),sQuery(id+"F0.wireOp",EDGE,"E23"),sQuery(id+"F0.wireOp",EDGE,"E24"),sQuery(id+"F0.wireOp",EDGE,"E25")])]});
            hole(context, id + "F12", {"style" : HoleStyle.SIMPLE, "endStyle" : HoleEndStyle.BLIND, "oppositeDirection" : true, "holeDiameter" : 9 * mm, "majorDiameter" : 5 * mm, "holeDepth" : 7 * mm, "isTappedThrough" : true, "tappedDepth" : 12 * mm, "tapClearance" : 3, "startFromSketch" : true, "locations" : qUnion([Q0, Q1, Q2]), "scope" : qUnion([Q3])});
        }
    });
